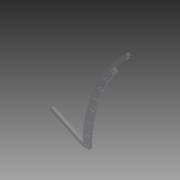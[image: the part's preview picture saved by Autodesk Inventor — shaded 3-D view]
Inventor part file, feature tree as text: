
AUTODESK INVENTOR PART (.ipt)
format: ipt  version: 2013 (Build 170138000, 138)  size: 120,832 bytes
history: native  units: in
note: dims shown in document units (in); Inventor stores cm internally (conversion verified against a paired STEP export)
features: extrude x2, sketch x2, reference x2
ambient origin geometry x8: Origin, YZ Plane, XZ Plane, XY Plane, X Axis, Y Axis, Z Axis, Center Point
bodies: Solid1 (feature_tree)
feature tree (6):
  extrude  "Extrusion1"  TaperAngle=45.0deg  [1 undecoded]
  extrude  "Extrusion2"  Depth=0.25in
  sketch  "Sketch1"  dims[d8=0.25in d9=0.0in d10=45.0deg]
  sketch  "Sketch5"  dims[d11=0.25in d12=0.25in d13=0.1718in d14=0.25in d15=3.0in d16=23.375in d18=0.125in d19=1.75in d20=1.0in d21=0.0in]
  reference  "Reference3"
  reference  "Reference4"
note: 1 required parameter value undecoded (feature->parameter linkage not recoverable at this tier; creation-order binding heuristic only, values carry confidence <= 0.55)
